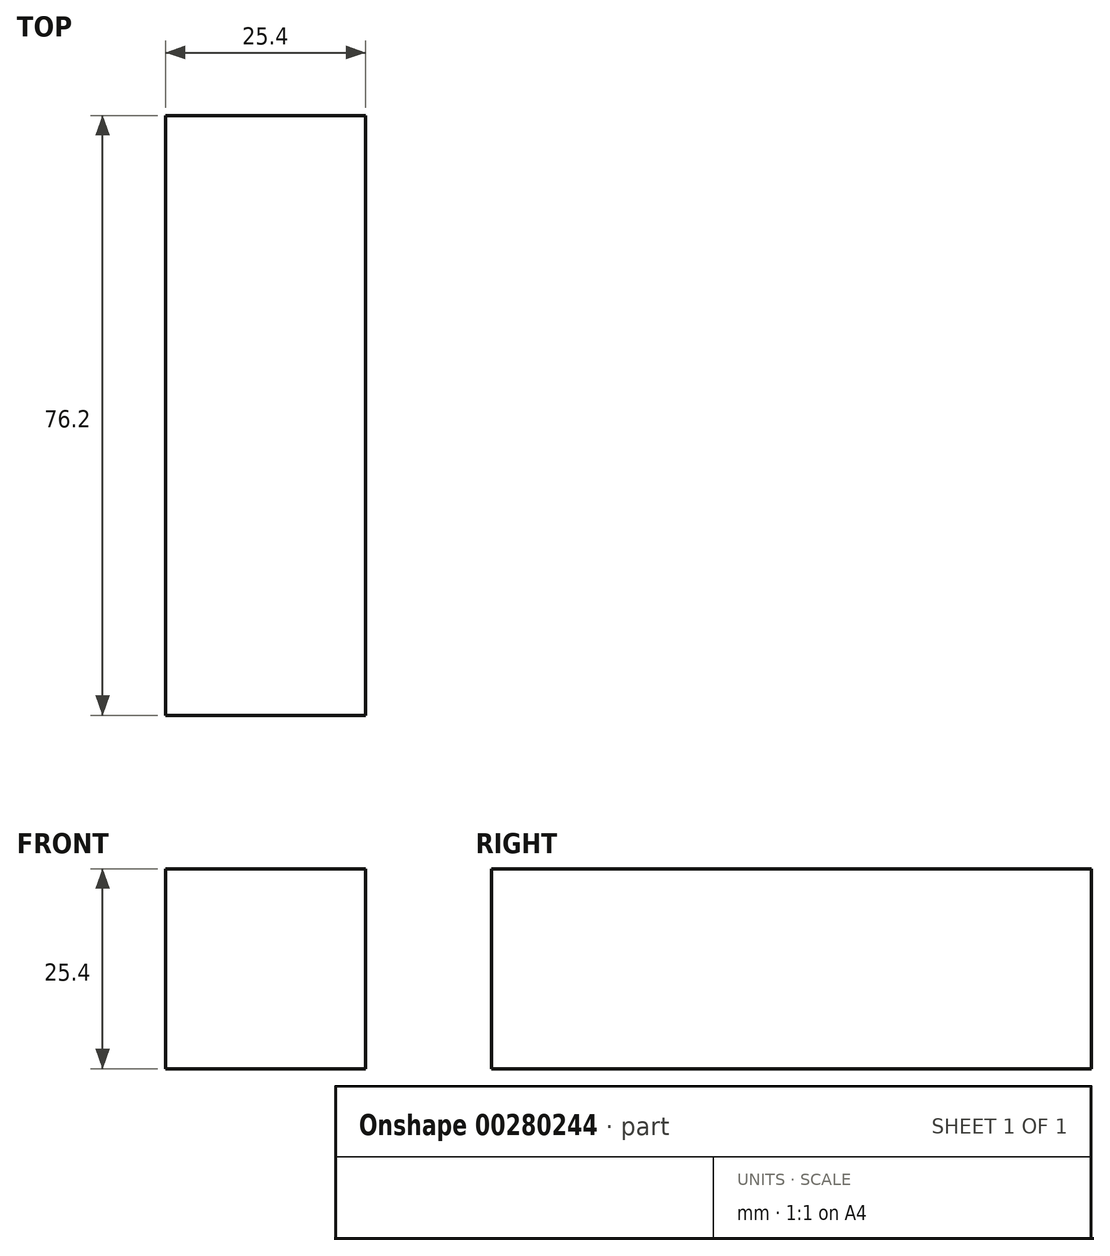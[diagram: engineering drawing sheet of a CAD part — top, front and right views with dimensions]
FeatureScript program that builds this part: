
annotation { "Feature Type Name" : "Feature", "Feature Type Description" : "" }
export const myFeature = defineFeature(function(context is Context, id is Id, definition is map)
    precondition{}
    {
        {
            var Q0;
            Q0=qCreatedBy(makeId("Front.planeOp"),FACE);
            var sketch = newSketch(context, id + "F0", { "sketchPlane" : qUnion([Q0])});
            skLineSegment(sketch, "E0.bottom", {"start": v(0, 0) * mm, "end": v(-25.4, 0) * mm});
            skLineSegment(sketch, "E0.top", {"start": v(0, 25.4) * mm, "end": v(-25.4, 25.4) * mm});
            skLineSegment(sketch, "E0.left", {"start": v(0, 0) * mm, "end": v(0, 25.4) * mm});
            skLineSegment(sketch, "E0.right", {"start": v(-25.4, 0) * mm, "end": v(-25.4, 25.4) * mm});
            skSolve(sketch);
        }
        {
            var Q0;
            Q0 = qSketchRegion(id + "F0", true);
            extrude(context, id + "F1", {"entities" : qUnion([Q0]), "depth" : 76.2 * mm});
        }
    });
